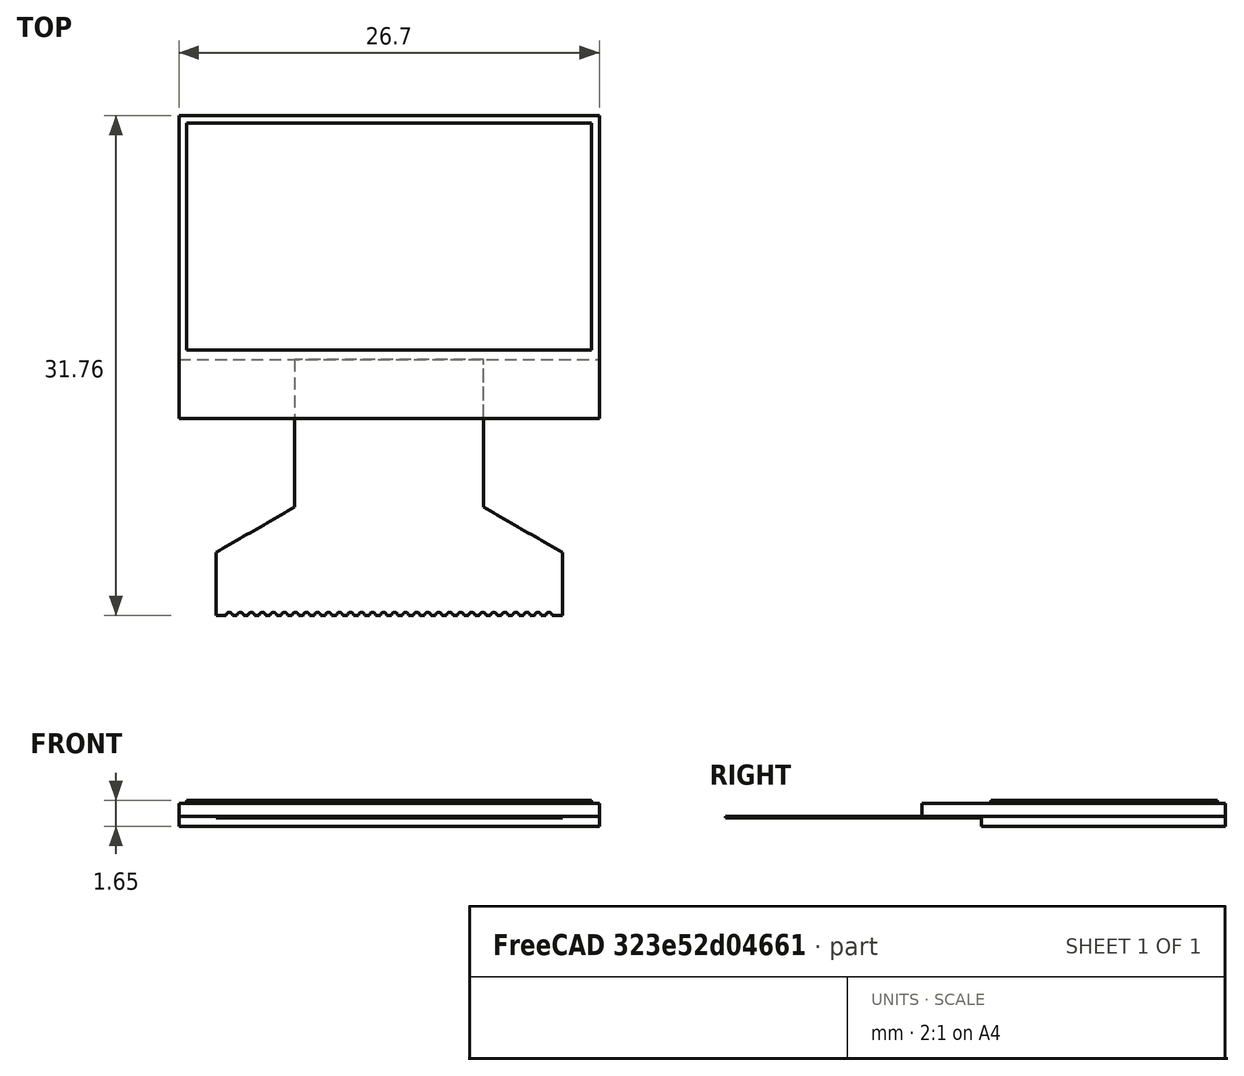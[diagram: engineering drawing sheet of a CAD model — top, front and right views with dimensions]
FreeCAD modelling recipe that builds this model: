
FCSTD DOCUMENT  (FreeCAD 0.18R16131 (Git))
Label: oled
License: All rights reserved
LicenseURL: http://en.wikipedia.org/wiki/All_rights_reserved
objects: Part::Box×3, Part::Feature×1, Part::Extrusion×1, App::DocumentObjectGroup×1
note: 5 computed .brp shape members not serialized (recipe doc carries the construction recipe); baked Part::Feature solids carry a one-line shape summary decoded from their .brp

FEATURE [Part::Box] Box  label="Panel"
  AttacherType = Attacher::AttachEngine3D
  Height = 0.817773
  Length = 26.7
  Placement = pos=(0,0,0.632227) rot=(0,0,1;0rad)
  Width = 19.26
FEATURE [Part::Box] Box001  label="Polarizer"
  AttacherType = Attacher::AttachEngine3D
  Height = 0.2
  Length = 25.7
  Placement = pos=(0.5,4.36,1.45) rot=(0,0,1;0rad)
  Width = 14.4
FEATURE [Part::Box] Box002  label="Cap"
  AttacherType = Attacher::AttachEngine3D
  Height = 0.632227
  Length = 26.7
  Placement = pos=(0,3.76,0) rot=(0,0,1;0rad)
  Width = 15.5
FEATURE [Part::Feature] path817
  shape: bbox 22 x 16.26 x 2e-07 mm, 1 faces, 0 solids (baked)
FEATURE [Part::Extrusion] Extrude
  Base = -> path817
  Dir = (0,0,1)
  DirMode = 0
  FaceMakerClass = Part::FaceMakerBullseye
  LengthFwd = 0.1
  LengthRev = 0
  Placement = pos=(2.35,3.76,0.53) rot=(0,0,1;0rad)
  Solid = true
  Symmetric = false
FEATURE [App::DocumentObjectGroup] Group
  Group = -> [Box001,Box,Box002,Extrude]
